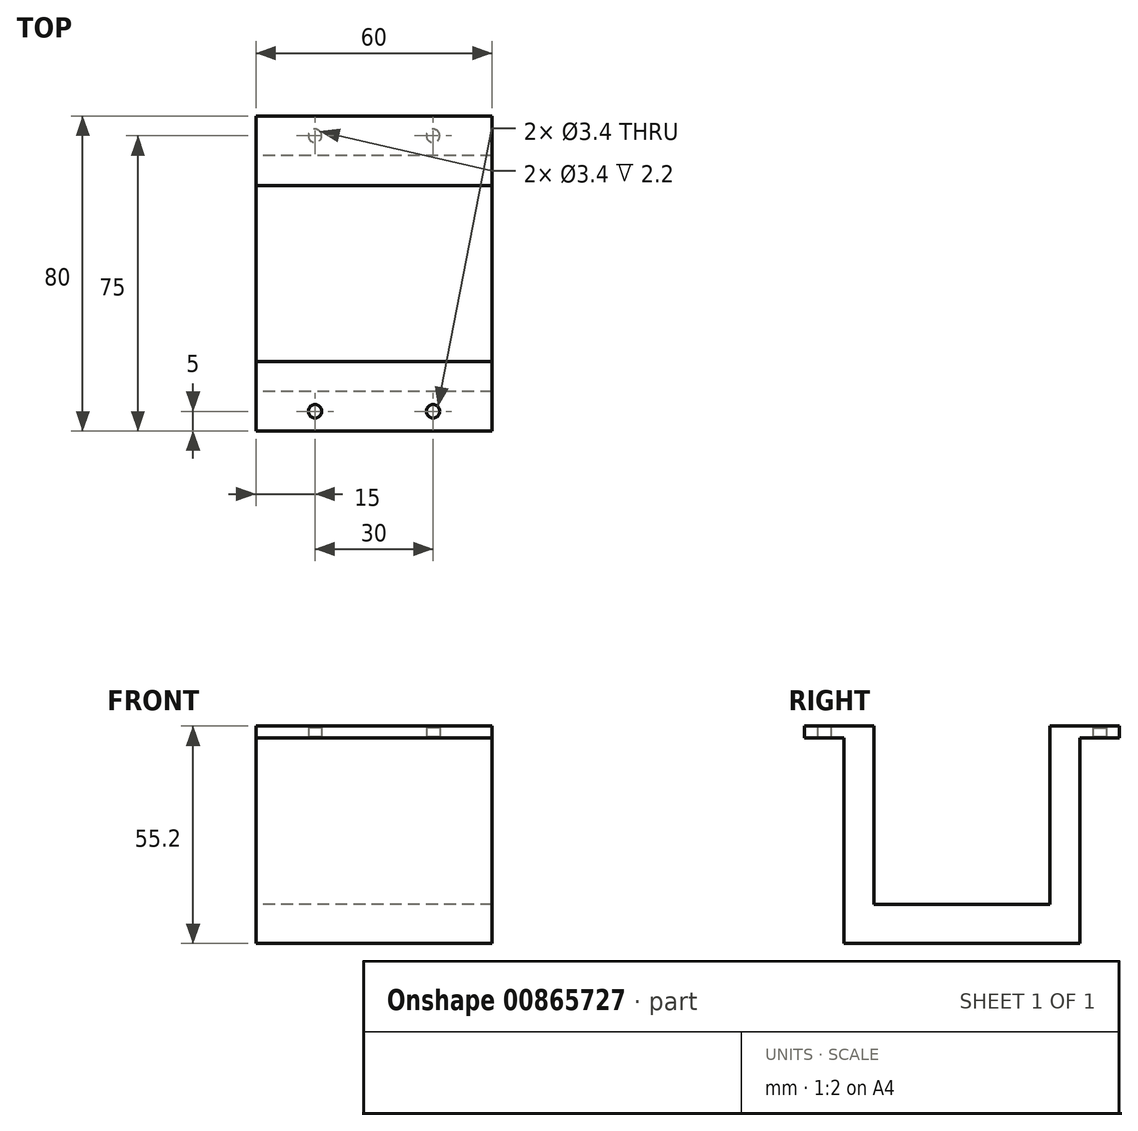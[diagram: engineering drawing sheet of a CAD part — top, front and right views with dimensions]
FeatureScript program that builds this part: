
annotation { "Feature Type Name" : "Feature", "Feature Type Description" : "" }
export const myFeature = defineFeature(function(context is Context, id is Id, definition is map)
    precondition{}
    {
        {
            var Q0;
            Q0=qCreatedBy(makeId("Top.planeOp"),FACE);
            var sketch = newSketch(context, id + "F0", { "sketchPlane" : qUnion([Q0])});
            skPoint(sketch, "E0.middle", {"position": v(0, 0) * mm});
            skLineSegment(sketch, "E1.bottom", {"start": v(30, -30) * mm, "end": v(-30, -30) * mm});
            skLineSegment(sketch, "E1.top", {"start": v(30, 30) * mm, "end": v(-30, 30) * mm});
            skLineSegment(sketch, "E1.left", {"start": v(30, -30) * mm, "end": v(30, 30) * mm});
            skLineSegment(sketch, "E1.right", {"start": v(-30, -30) * mm, "end": v(-30, 30) * mm});
            skLineSegment(sketch, "E2.bottom", {"start": v(30, -22.4) * mm, "end": v(-30, -22.4) * mm});
            skLineSegment(sketch, "E2.top", {"start": v(30, 22.4) * mm, "end": v(-30, 22.4) * mm});
            skLineSegment(sketch, "E2.left", {"start": v(30, -22.4) * mm, "end": v(30, 22.4) * mm});
            skLineSegment(sketch, "E2.right", {"start": v(-30, -22.4) * mm, "end": v(-30, 22.4) * mm});
            skLineSegment(sketch, "E3.bottom", {"start": v(30, -40) * mm, "end": v(-30, -40) * mm});
            skLineSegment(sketch, "E3.top", {"start": v(30, 40) * mm, "end": v(-30, 40) * mm});
            skLineSegment(sketch, "E3.left", {"start": v(30, -40) * mm, "end": v(30, 40) * mm});
            skLineSegment(sketch, "E3.right", {"start": v(-30, -40) * mm, "end": v(-30, 40) * mm});
            skCircle(sketch, "E4", {"center": v(-15, 35) * mm, "radius": 1.7 * mm});
            skCircle(sketch, "E5", {"center": v(15, 35) * mm, "radius": 1.7 * mm});
            skCircle(sketch, "E6.MirrorC", {"center": v(15, -35) * mm, "radius": 1.7 * mm});
            skCircle(sketch, "E7.MirrorC", {"center": v(-15, -35) * mm, "radius": 1.7 * mm});
            skSolve(sketch);
        }
        {
            var Q0;
            {var subQ0=sQuery(id+"F0.wireOp",EDGE,"E2.bottom");Q0=makeQuery(id+"F0.imprint","IMPRINT",FACE,{"disambiguationData":[TD([[makeQuery(id+"F0.imprint","IMPRINT",EDGE,{"derivedFrom":subQ0}),-1.0]])]});}
            extrude(context, id + "F1", {"entities" : qUnion([Q0]), "depth" : 9.9 * mm, "offsetDistance" : 25.4 * mm});
        }
        {
            var Q0;
            {var subQ0=sQuery(id+"F0.wireOp",EDGE,"E1.bottom");Q0=makeQuery(id+"F0.imprint","IMPRINT",FACE,{"disambiguationData":[TD([[makeQuery(id+"F0.imprint","IMPRINT",EDGE,{"derivedFrom":subQ0}),-1.0]])]});}
            var Q1;
            {var subQ0=sQuery(id+"F0.wireOp",EDGE,"E1.top");Q1=makeQuery(id+"F0.imprint","IMPRINT",FACE,{"disambiguationData":[TD([[makeQuery(id+"F0.imprint","IMPRINT",EDGE,{"derivedFrom":subQ0}),1.0]])]});}
            extrude(context, id + "F2", {"entities" : qUnion([Q0, Q1]), "operationType" : NewBodyOperationType.ADD, "depth" : 55.2 * mm, "offsetDistance" : 25.4 * mm});
        }
        {
            var Q0;
            {var subQ0=sQuery(id+"F0.wireOp",EDGE,"E1.top");Q0=makeQuery(id+"F0.imprint","IMPRINT",FACE,{"disambiguationData":[TD([[makeQuery(id+"F0.imprint","IMPRINT",EDGE,{"derivedFrom":subQ0}),-1.0]])]});}
            var Q1;
            {var subQ0=sQuery(id+"F0.wireOp",EDGE,"E1.bottom");Q1=makeQuery(id+"F0.imprint","IMPRINT",FACE,{"disambiguationData":[TD([[makeQuery(id+"F0.imprint","IMPRINT",EDGE,{"derivedFrom":subQ0}),1.0]])]});}
            extrude(context, id + "F3", {"entities" : qUnion([Q0, Q1]), "operationType" : NewBodyOperationType.ADD, "depth" : 55.2 * mm, "offsetDistance" : 25.4 * mm, "hasSecondDirection" : true, "secondDirectionOppositeDirection" : true, "secondDirectionDepth" : -52.2 * mm});
        }
        {
            var Q0;
            Q0=makeQuery(id+"F0.imprint","IMPRINT",FACE,{"disambiguationData":[TD([[makeQuery(id+"F0.imprint","IMPRINT",EDGE,{"derivedFrom":sQuery(id+"F0.wireOp",EDGE,"E4")}),1.0]])]});
            var Q1;
            Q1=makeQuery(id+"F0.imprint","IMPRINT",FACE,{"disambiguationData":[TD([[makeQuery(id+"F0.imprint","IMPRINT",EDGE,{"derivedFrom":sQuery(id+"F0.wireOp",EDGE,"E5")}),1.0]])]});
            var Q2;
            Q2=makeQuery(id+"F0.imprint","IMPRINT",FACE,{"disambiguationData":[TD([[makeQuery(id+"F0.imprint","IMPRINT",EDGE,{"derivedFrom":sQuery(id+"F0.wireOp",EDGE,"E7.MirrorC")}),-1.0]])]});
            var Q3;
            Q3=makeQuery(id+"F0.imprint","IMPRINT",FACE,{"disambiguationData":[TD([[makeQuery(id+"F0.imprint","IMPRINT",EDGE,{"derivedFrom":sQuery(id+"F0.wireOp",EDGE,"E6.MirrorC")}),-1.0]])]});
            extrude(context, id + "F4", {"entities" : qUnion([Q0, Q1, Q2, Q3]), "operationType" : NewBodyOperationType.ADD, "depth" : 52.5 * mm, "offsetDistance" : 25.4 * mm, "hasSecondDirection" : true, "secondDirectionOppositeDirection" : true, "secondDirectionDepth" : -52.2 * mm});
        }
        {
            var Q0;
            Q0=makeQuery(id+"F0.imprint","IMPRINT",FACE,{"disambiguationData":[TD([[makeQuery(id+"F0.imprint","IMPRINT",EDGE,{"derivedFrom":sQuery(id+"F0.wireOp",EDGE,"E4")}),1.0]])]});
            var Q1;
            Q1=makeQuery(id+"F0.imprint","IMPRINT",FACE,{"disambiguationData":[TD([[makeQuery(id+"F0.imprint","IMPRINT",EDGE,{"derivedFrom":sQuery(id+"F0.wireOp",EDGE,"E5")}),1.0]])]});
            var Q2;
            Q2=makeQuery(id+"F0.imprint","IMPRINT",FACE,{"disambiguationData":[TD([[makeQuery(id+"F0.imprint","IMPRINT",EDGE,{"derivedFrom":sQuery(id+"F0.wireOp",EDGE,"E7.MirrorC")}),-1.0]])]});
            var Q3;
            Q3=makeQuery(id+"F0.imprint","IMPRINT",FACE,{"disambiguationData":[TD([[makeQuery(id+"F0.imprint","IMPRINT",EDGE,{"derivedFrom":sQuery(id+"F0.wireOp",EDGE,"E6.MirrorC")}),-1.0]])]});
            extrude(context, id + "F5", {"entities" : qUnion([Q0, Q1, Q2, Q3]), "operationType" : NewBodyOperationType.ADD, "depth" : 55.2 * mm, "offsetDistance" : 25.4 * mm, "hasSecondDirection" : true, "secondDirectionOppositeDirection" : true, "secondDirectionDepth" : -54.7 * mm});
        }
    });
